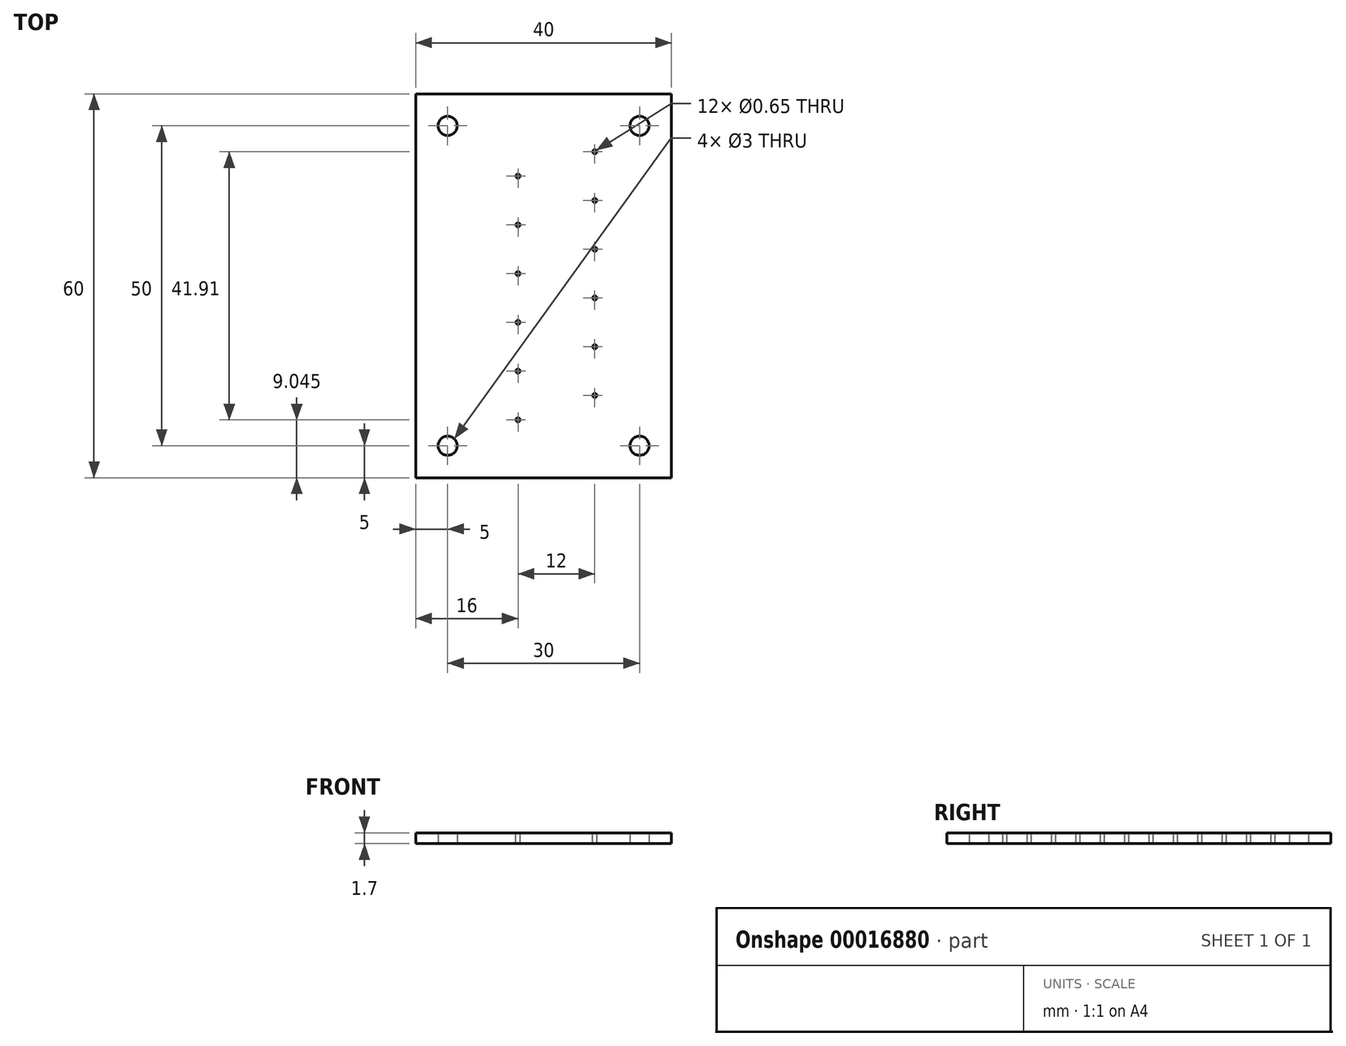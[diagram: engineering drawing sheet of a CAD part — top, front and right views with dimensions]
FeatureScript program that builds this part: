
annotation { "Feature Type Name" : "Feature", "Feature Type Description" : "" }
export const myFeature = defineFeature(function(context is Context, id is Id, definition is map)
    precondition{}
    {
        {
            var Q0;
            Q0=qCreatedBy(makeId("Top.planeOp"),FACE);
            var sketch = newSketch(context, id + "F0", { "sketchPlane" : qUnion([Q0])});
            skLineSegment(sketch, "E0", {"start": v(0, 0) * mm, "end": v(40, 0) * mm});
            skLineSegment(sketch, "E1", {"start": v(40, 0) * mm, "end": v(40, 60) * mm});
            skLineSegment(sketch, "E2", {"start": v(0, 60) * mm, "end": v(0, 0) * mm});
            skLineSegment(sketch, "E3", {"start": v(40, 60) * mm, "end": v(0, 60) * mm});
            skSolve(sketch);
        }
        {
            var Q0;
            Q0 = qSketchRegion(id + "F0", true);
            extrude(context, id + "F1", {"entities" : qUnion([Q0]), "depth" : 1.7 * mm});
        }
        {
            var Q0;
            Q0=qCreatedBy(makeId("Top.planeOp"),FACE);
            var sketch = newSketch(context, id + "F2", { "sketchPlane" : qUnion([Q0])});
            skLineSegment(sketch, "E4.0", {"start": v(0, 0) * mm, "end": v(40, 0) * mm});
            skLineSegment(sketch, "E5", {"start": v(5, 0) * mm, "end": v(5, 63.3) * mm, "construction": true});
            skCircle(sketch, "E6", {"center": v(5, 5) * mm, "radius": 1.5 * mm});
            skCircle(sketch, "E7", {"center": v(5, 55) * mm, "radius": 1.5 * mm});
            skLineSegment(sketch, "E8", {"start": v(20, 0) * mm, "end": v(20, 70.02) * mm, "construction": true});
            skCircle(sketch, "E9.MirrorC", {"center": v(35, 55) * mm, "radius": 1.5 * mm});
            skCircle(sketch, "E10.MirrorC", {"center": v(35, 5) * mm, "radius": 1.5 * mm});
            skSolve(sketch);
        }
        {
            var Q0;
            Q0 = qSketchRegion(id + "F2", true);
            extrude(context, id + "F3", {"entities" : qUnion([Q0]), "operationType" : NewBodyOperationType.REMOVE, "depth" : 25 * mm});
        }
        {
            var Q0;
            Q0=makeQuery(id+"F1.opExtrude","CAP_FACE",FACE,{"disambiguationData":[OSD([sQuery(id+"F0.wireOp",EDGE,"E0"),sQuery(id+"F0.wireOp",EDGE,"E1"),sQuery(id+"F0.wireOp",EDGE,"E2"),sQuery(id+"F0.wireOp",EDGE,"E3")])],"isStart":false});
            var sketch = newSketch(context, id + "F4", { "sketchPlane" : qUnion([Q0])});
            skLineSegment(sketch, "E11", {"start": v(40, 30) * mm, "end": v(0, 30) * mm, "construction": true});
            skLineSegment(sketch, "E12", {"start": v(28, 60) * mm, "end": v(28, 0) * mm, "construction": true});
            skLineSegment(sketch, "E13", {"start": v(16, 60) * mm, "end": v(16, 0) * mm, "construction": true});
            skLineSegment(sketch, "E14", {"start": v(40, 31.9) * mm, "end": v(0, 31.9) * mm, "construction": true});
            skLineSegment(sketch, "E15.0.1.0", {"start": v(40, 35.71) * mm, "end": v(0, 35.71) * mm, "construction": true});
            skLineSegment(sketch, "E15.0.2.0", {"start": v(40, 39.52) * mm, "end": v(0, 39.52) * mm, "construction": true});
            skLineSegment(sketch, "E15.0.3.0", {"start": v(40, 43.34) * mm, "end": v(0, 43.34) * mm, "construction": true});
            skLineSegment(sketch, "E15.0.4.0", {"start": v(40, 47.14) * mm, "end": v(0, 47.14) * mm, "construction": true});
            skLineSegment(sketch, "E15.0.5.0", {"start": v(40, 50.95) * mm, "end": v(0, 50.95) * mm, "construction": true});
            skLineSegment(sketch, "E15.direction1", {"start": v(0, 31.9) * mm, "end": v(25, 31.9) * mm, "construction": true});
            skLineSegment(sketch, "E15.direction2", {"start": v(0, 31.9) * mm, "end": v(0, 35.71) * mm, "construction": true});
            skLineSegment(sketch, "E16.MirrorCS", {"start": v(0, 28.1) * mm, "end": v(25, 28.1) * mm, "construction": true});
            skLineSegment(sketch, "E17.MirrorCS", {"start": v(40, 24.28) * mm, "end": v(0, 24.29) * mm, "construction": true});
            skLineSegment(sketch, "E18.MirrorCS", {"start": v(40, 20.47) * mm, "end": v(0, 20.48) * mm, "construction": true});
            skLineSegment(sketch, "E19.MirrorCS", {"start": v(40, 16.66) * mm, "end": v(0, 16.67) * mm, "construction": true});
            skLineSegment(sketch, "E20.MirrorCS", {"start": v(40, 12.85) * mm, "end": v(0, 12.86) * mm, "construction": true});
            skLineSegment(sketch, "E21.MirrorCS", {"start": v(40, 9.04) * mm, "end": v(0, 9.04) * mm, "construction": true});
            skLineSegment(sketch, "E22.MirrorCS", {"start": v(40, 28.1) * mm, "end": v(0, 28.1) * mm, "construction": true});
            skCircle(sketch, "E23", {"center": v(16, 9.04) * mm, "radius": 0.33 * mm});
            skCircle(sketch, "E24", {"center": v(28, 12.85) * mm, "radius": 0.33 * mm});
            skCircle(sketch, "E25.0.1.0", {"center": v(16, 16.66) * mm, "radius": 0.33 * mm});
            skCircle(sketch, "E25.0.2.0", {"center": v(16, 24.29) * mm, "radius": 0.33 * mm});
            skCircle(sketch, "E25.0.3.0", {"center": v(16, 31.9) * mm, "radius": 0.33 * mm});
            skCircle(sketch, "E25.0.4.0", {"center": v(16, 39.53) * mm, "radius": 0.33 * mm});
            skCircle(sketch, "E25.0.5.0", {"center": v(16, 47.15) * mm, "radius": 0.33 * mm});
            skLineSegment(sketch, "E25.direction1", {"start": v(16, 9.04) * mm, "end": v(41, 9.04) * mm, "construction": true});
            skLineSegment(sketch, "E25.direction2", {"start": v(16, 9.04) * mm, "end": v(16, 16.66) * mm, "construction": true});
            skCircle(sketch, "E26.0.1.0", {"center": v(28, 20.47) * mm, "radius": 0.33 * mm});
            skCircle(sketch, "E26.0.2.0", {"center": v(28, 28.1) * mm, "radius": 0.33 * mm});
            skCircle(sketch, "E26.0.3.0", {"center": v(28, 35.71) * mm, "radius": 0.33 * mm});
            skCircle(sketch, "E26.0.4.0", {"center": v(28, 43.33) * mm, "radius": 0.33 * mm});
            skCircle(sketch, "E26.0.5.0", {"center": v(28, 50.95) * mm, "radius": 0.33 * mm});
            skLineSegment(sketch, "E26.direction1", {"start": v(28, 12.85) * mm, "end": v(53, 12.85) * mm, "construction": true});
            skLineSegment(sketch, "E26.direction2", {"start": v(28, 12.85) * mm, "end": v(28, 20.47) * mm, "construction": true});
            skSolve(sketch);
        }
        {
            var Q0;
            Q0 = qSketchRegion(id + "F4", true);
            extrude(context, id + "F5", {"entities" : qUnion([Q0]), "operationType" : NewBodyOperationType.REMOVE, "endBound" : BoundingType.THROUGH_ALL, "oppositeDirection" : true, "depth" : 25 * mm});
        }
    });
